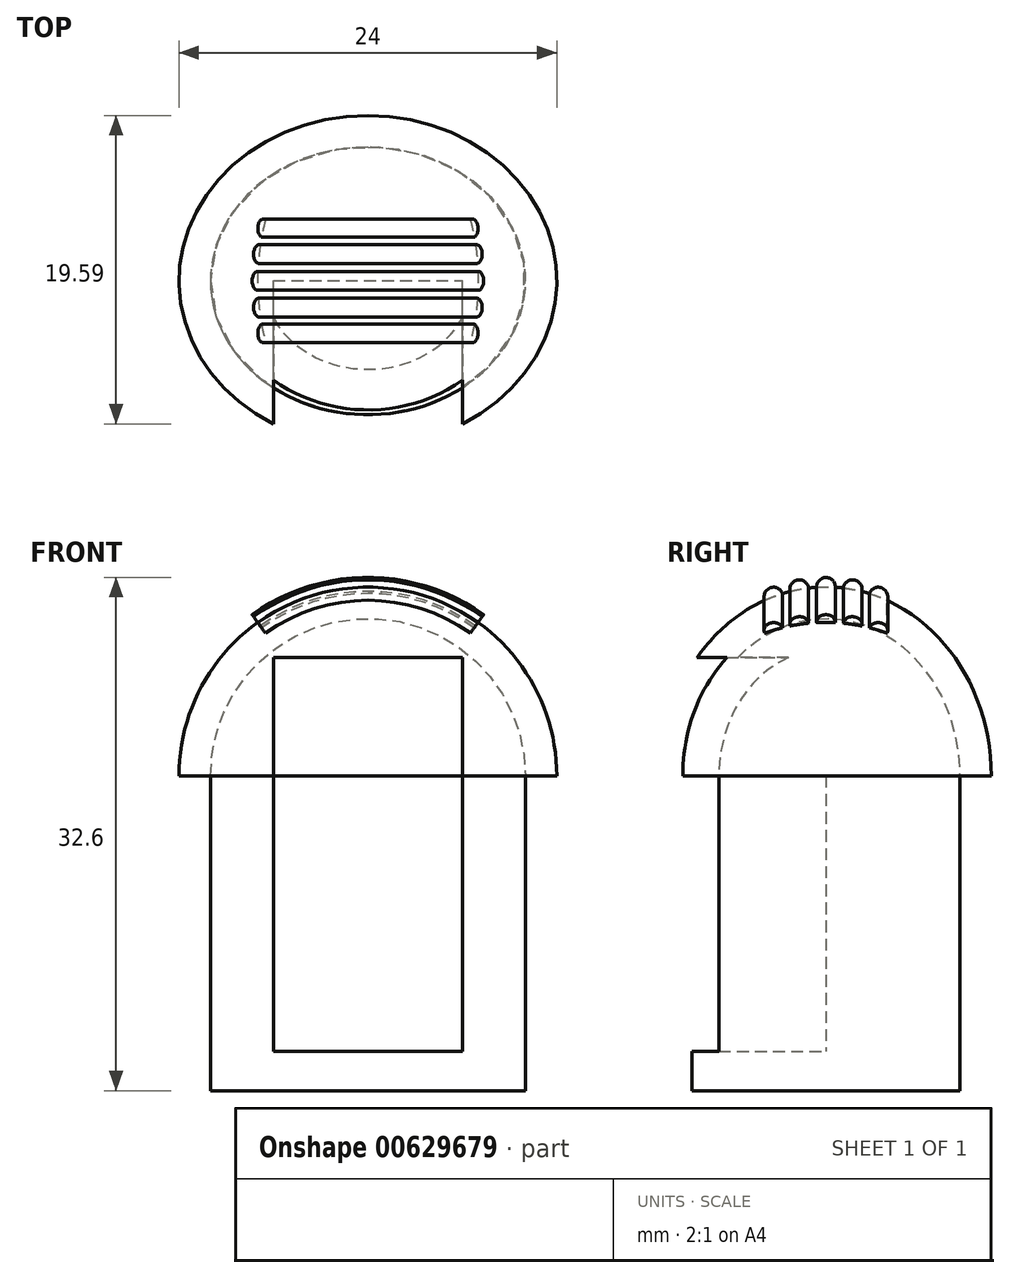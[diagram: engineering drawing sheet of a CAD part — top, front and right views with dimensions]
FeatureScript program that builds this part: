
annotation { "Feature Type Name" : "Feature", "Feature Type Description" : "" }
export const myFeature = defineFeature(function(context is Context, id is Id, definition is map)
    precondition{}
    {
        {
            var Q0;
            Q0=qCreatedBy(makeId("Top.planeOp"),FACE);
            var sketch = newSketch(context, id + "F0", { "sketchPlane" : qUnion([Q0])});
            skEllipse(sketch, "E0", {"center": v(0, 0) * mm, "majorRadius": 10 * mm, "minorRadius": 8.5 * mm, "majorAxis": v(-1, 0)});
            skFitSpline(sketch, "E1.0", {"points": [v(-11.96, 1.07) * mm, v(-12.02, 0) * mm, v(-11.96, -1.07) * mm, v(-11.71, -2.47) * mm, v(-11.23, -3.82) * mm, v(-10.53, -5.08) * mm, v(-9.7, -6.27) * mm, v(-8.42, -7.58) * mm, v(-6.9, -8.65) * mm, v(-5.55, -9.33) * mm, v(-4.14, -9.9) * mm, v(-2.67, -10.28) * mm, v(-1.15, -10.47) * mm, v(0, -10.52) * mm, v(1.15, -10.47) * mm, v(2.67, -10.28) * mm, v(4.14, -9.9) * mm, v(5.55, -9.33) * mm, v(6.9, -8.65) * mm, v(8.42, -7.58) * mm, v(9.7, -6.27) * mm, v(10.53, -5.08) * mm, v(11.23, -3.82) * mm, v(11.71, -2.47) * mm, v(11.96, -1.07) * mm, v(12.02, 0) * mm, v(11.96, 1.07) * mm, v(11.71, 2.47) * mm, v(11.23, 3.82) * mm, v(10.53, 5.08) * mm, v(9.7, 6.27) * mm, v(8.42, 7.58) * mm, v(6.9, 8.65) * mm, v(5.55, 9.33) * mm, v(4.14, 9.9) * mm, v(2.67, 10.28) * mm, v(1.15, 10.47) * mm, v(0, 10.52) * mm, v(-1.15, 10.47) * mm, v(-2.67, 10.28) * mm, v(-4.14, 9.9) * mm, v(-5.55, 9.33) * mm, v(-6.9, 8.65) * mm, v(-8.42, 7.58) * mm, v(-9.7, 6.27) * mm, v(-10.53, 5.08) * mm, v(-11.23, 3.82) * mm, v(-11.71, 2.47) * mm, v(-11.96, 1.07) * mm, v(-12.02, 0) * mm, v(-11.96, -1.07) * mm, v(-11.96, 1.07) * mm]});
            skSolve(sketch);
        }
        {
            var Q0;
            Q0=qSketchRegion(id+"F0",true);
            extrude(context, id + "F1", {"entities" : qUnion([Q0]), "depth" : 20 * mm, "offsetDistance" : 25 * mm});
        }
        {
            var Q0;
            Q0=makeQuery(id+"F1.opExtrude","CAP_FACE",FACE,{"disambiguationData":[OSD([sQuery(id+"F0.wireOp",EDGE,"E0")])],"isStart":false});
            var sketch = newSketch(context, id + "F2", { "sketchPlane" : qUnion([Q0])});
            skEllipticalArc(sketch, "E2", {});
            skLineSegment(sketch, "E3", {"start": v(0, -10.5) * mm, "end": v(0, 10.5) * mm, "construction": true});
            skLineSegment(sketch, "E4", {"start": v(-12, 0) * mm, "end": v(12, 0) * mm, "construction": true});
            skPoint(sketch, "E4.endSnap0", {"position": v(10, 0) * mm});
            skEllipticalArc(sketch, "E5", {});
            skLineSegment(sketch, "E6", {"start": v(0, 10.5) * mm, "end": v(0, 8.5) * mm});
            skLineSegment(sketch, "E7", {"start": v(0, -8.5) * mm, "end": v(0, -10.5) * mm});
            const initialGuessF2  = {"E2": [0, 0, -1, 0, 0.01, 0.0085, 4.71238898038469, 1.5707963267948966], "E5": [0, 0, -1, 0, 0.012, 0.0105, 4.71238898038469, 3.141592653589793]};
            skSetInitialGuess(sketch, initialGuessF2);
            skSolve(sketch);
        }
        {
            var Q0;
            Q0=makeQuery(id+"F2.imprint","IMPRINT",FACE,{"disambiguationData":[TD([[makeQuery(id+"F2.imprint","IMPRINT",EDGE,{"derivedFrom":sQuery(id+"F2.wireOp",EDGE,"E2")}),-1.0]])]});
            var Q1;
            Q1=sQuery(id+"F2.wireOp",EDGE,"E3");
            revolve(context, id + "F3", {"entities" : qUnion([Q0]), "axis" : qUnion([Q1]), "revolveType" : RevolveType.ONE_DIRECTION, "angle" : 180 * degree});
        }
        {
            var Q0;
            Q0=qCreatedBy(makeId("Front.planeOp"),FACE);
            var sketch = newSketch(context, id + "F4", { "sketchPlane" : qUnion([Q0])});
            skPoint(sketch, "E8.center.orphan", {"position": v(0, 0) * mm});
            skLineSegment(sketch, "E9.bottom", {"start": v(-6, 27.5) * mm, "end": v(6, 27.5) * mm});
            skLineSegment(sketch, "E9.top", {"start": v(-6, 2.5) * mm, "end": v(6, 2.5) * mm});
            skLineSegment(sketch, "E9.left", {"start": v(-6, 27.5) * mm, "end": v(-6, 2.5) * mm});
            skLineSegment(sketch, "E9.right", {"start": v(6, 27.5) * mm, "end": v(6, 2.5) * mm});
            skSolve(sketch);
        }
        {
            var Q0;
            Q0=qSketchRegion(id+"F4",true);
            extrude(context, id + "F5", {"entities" : qUnion([Q0]), "operationType" : NewBodyOperationType.REMOVE, "endBound" : BoundingType.THROUGH_ALL, "depth" : 25 * mm, "offsetDistance" : 25 * mm});
        }
        {
            var Q0;
            Q0=qCreatedBy(makeId("Right.planeOp"),FACE);
            var sketch = newSketch(context, id + "F6", { "sketchPlane" : qUnion([Q0])});
            skLineSegment(sketch, "E10", {"start": v(-15.32, 20) * mm, "end": v(25.38, 20) * mm, "construction": true});
            skLineSegment(sketch, "E11", {"start": v(0, 40.59) * mm, "end": v(0, -14.26) * mm, "construction": true});
            skEllipticalArc(sketch, "E12", {});
            skArc(sketch, "E13", {"start": v(0.6, 31.98) * mm, "mid": v(0, 32.6) * mm, "end": v(-0.6, 31.98) * mm});
            skArc(sketch, "E14", {"start": v(-1.1, 31.93) * mm, "mid": v(-1.8, 32.43) * mm, "end": v(-2.28, 31.71) * mm});
            skArc(sketch, "E15", {"start": v(2.28, 31.71) * mm, "mid": v(1.8, 32.43) * mm, "end": v(1.1, 31.93) * mm});
            skArc(sketch, "E16", {"start": v(-2.76, 31.58) * mm, "mid": v(-3.54, 31.94) * mm, "end": v(-3.88, 31.15) * mm});
            skArc(sketch, "E17", {"start": v(3.88, 31.15) * mm, "mid": v(3.54, 31.94) * mm, "end": v(2.76, 31.58) * mm});
            const initialGuessF6  = {"E12": [0, 0.02, 1, 0, 0.0105, 0.012, 6.283185307179586, 3.141592653589793]};
            skSetInitialGuess(sketch, initialGuessF6);
            skSolve(sketch);
        }
        {
            var Q0;
            Q0=qCreatedBy(makeId("Front.planeOp"),FACE);
            var sketch = newSketch(context, id + "F7", { "sketchPlane" : qUnion([Q0])});
            skLineSegment(sketch, "E18", {"start": v(0, 0) * mm, "end": v(0, 37.2) * mm, "construction": true});
            skLineSegment(sketch, "E19", {"start": v(-20.52, 20) * mm, "end": v(37.24, 20) * mm, "construction": true});
            skEllipticalArc(sketch, "E20", {});
            skLineSegment(sketch, "E21", {"start": v(-7, 20) * mm, "end": v(-7, 29.75) * mm, "construction": true});
            skLineSegment(sketch, "E22", {"start": v(7, 20) * mm, "end": v(7, 29.75) * mm, "construction": true});
            const initialGuessF7  = {"E20": [0, 0.02, -1, 0, 0.012, 0.012, 4.0895623949726865, 5.335215565796693]};
            skSetInitialGuess(sketch, initialGuessF7);
            skSolve(sketch);
        }
        {
            var Q0;
            Q0 = qSketchRegion(id + "F6", true);
            var Q1;
            Q1=sQuery(id+"F7.wireOp",EDGE,"E20");
            sweep(context, id + "F8", {"profiles" : qUnion([Q0]), "path" : qUnion([Q1])});
        }
    });
